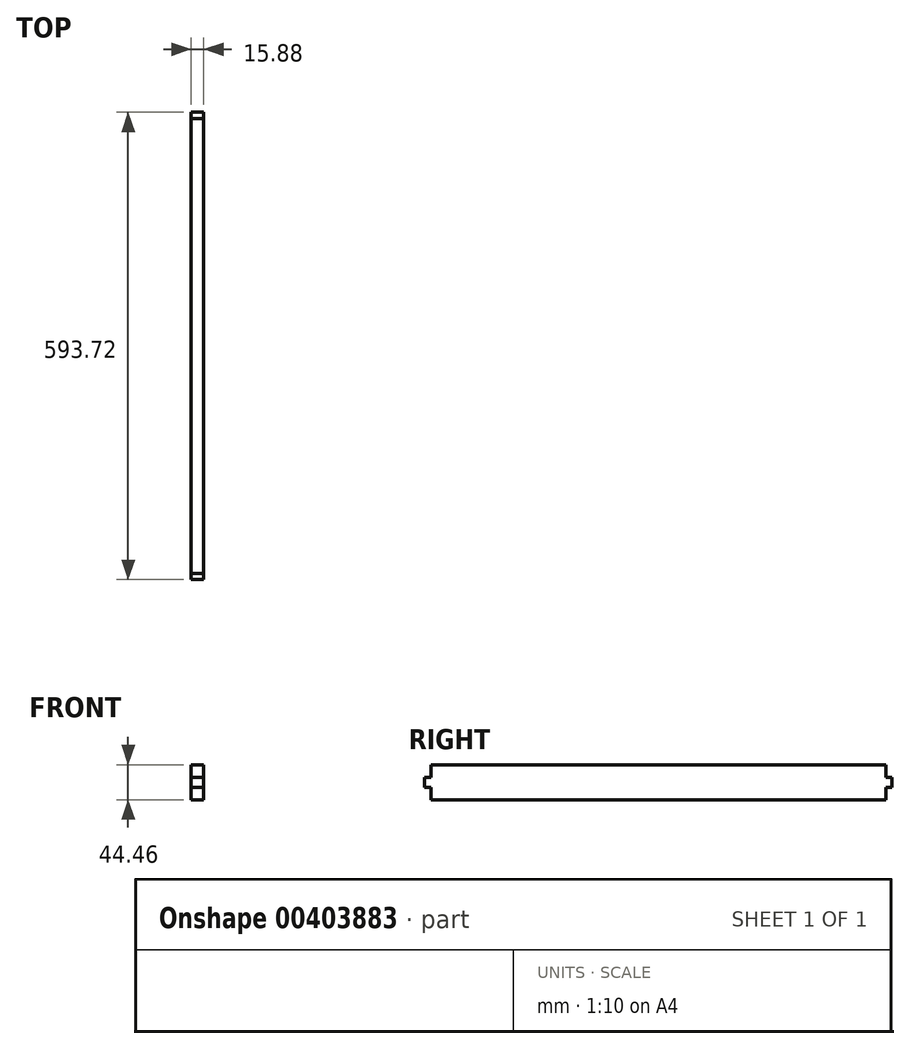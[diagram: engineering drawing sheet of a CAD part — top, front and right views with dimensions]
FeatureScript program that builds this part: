
annotation { "Feature Type Name" : "Feature", "Feature Type Description" : "" }
export const myFeature = defineFeature(function(context is Context, id is Id, definition is map)
    precondition{}
    {
        {
            var Q0;
            Q0=qCreatedBy(makeId("Right.planeOp"),FACE);
            var sketch = newSketch(context, id + "F0", { "sketchPlane" : qUnion([Q0])});
            skLineSegment(sketch, "E0.bottom", {"start": v(296.86, -22.23) * mm, "end": v(-296.86, -22.23) * mm});
            skLineSegment(sketch, "E0.top", {"start": v(296.86, 22.23) * mm, "end": v(-296.86, 22.22) * mm});
            skLineSegment(sketch, "E0.left", {"start": v(296.86, -22.23) * mm, "end": v(296.86, 22.22) * mm});
            skLineSegment(sketch, "E0.right", {"start": v(-296.86, -22.23) * mm, "end": v(-296.86, 22.22) * mm});
            skPoint(sketch, "E0.middle", {"position": v(0, 0) * mm});
            skSolve(sketch);
        }
        {
            var Q0;
            Q0 = qSketchRegion(id + "F0", true);
            extrude(context, id + "F1", {"entities" : qUnion([Q0]), "depth" : 15.88 * mm});
        }
        {
            var Q0;
            Q0=makeQuery(id+"F1.opExtrude","CAP_FACE",FACE,{"disambiguationData":[OSD([sQuery(id+"F0.wireOp",EDGE,"E0.bottom"),sQuery(id+"F0.wireOp",EDGE,"E0.top"),sQuery(id+"F0.wireOp",EDGE,"E0.left"),sQuery(id+"F0.wireOp",EDGE,"E0.right")])],"isStart":false});
            var sketch = newSketch(context, id + "F2", { "sketchPlane" : qUnion([Q0])});
            skLineSegment(sketch, "E1.bottom", {"start": v(-296.86, 22.22) * mm, "end": v(-288.93, 22.22) * mm});
            skLineSegment(sketch, "E1.top", {"start": v(-296.86, 6.35) * mm, "end": v(-288.93, 6.35) * mm});
            skLineSegment(sketch, "E1.left", {"start": v(-296.86, 22.22) * mm, "end": v(-296.86, 6.35) * mm});
            skLineSegment(sketch, "E1.right", {"start": v(-288.93, 22.22) * mm, "end": v(-288.93, 6.35) * mm});
            skLineSegment(sketch, "E2.bottom", {"start": v(-296.86, -22.23) * mm, "end": v(-288.93, -22.23) * mm});
            skLineSegment(sketch, "E2.top", {"start": v(-296.86, -6.35) * mm, "end": v(-288.93, -6.35) * mm});
            skLineSegment(sketch, "E2.left", {"start": v(-296.86, -22.23) * mm, "end": v(-296.86, -6.35) * mm});
            skLineSegment(sketch, "E2.right", {"start": v(-288.93, -22.23) * mm, "end": v(-288.93, -6.35) * mm});
            skLineSegment(sketch, "E3.MirrorCS", {"start": v(296.86, 22.22) * mm, "end": v(288.93, 22.22) * mm});
            skLineSegment(sketch, "E4.MirrorCS", {"start": v(296.86, 6.35) * mm, "end": v(288.93, 6.35) * mm});
            skLineSegment(sketch, "E5.MirrorCS", {"start": v(288.93, -22.23) * mm, "end": v(288.93, -6.35) * mm});
            skLineSegment(sketch, "E6.MirrorCS", {"start": v(296.86, 22.22) * mm, "end": v(296.86, 6.35) * mm});
            skLineSegment(sketch, "E7.MirrorCS", {"start": v(288.93, 22.22) * mm, "end": v(288.93, 6.35) * mm});
            skLineSegment(sketch, "E8.MirrorCS", {"start": v(296.86, -22.23) * mm, "end": v(288.93, -22.23) * mm});
            skLineSegment(sketch, "E9.MirrorCS", {"start": v(296.86, -22.23) * mm, "end": v(296.86, -6.35) * mm});
            skLineSegment(sketch, "E10.MirrorCS", {"start": v(296.86, -6.35) * mm, "end": v(288.93, -6.35) * mm});
            skSolve(sketch);
        }
        {
            var Q0;
            Q0 = qSketchRegion(id + "F2", true);
            extrude(context, id + "F3", {"entities" : qUnion([Q0]), "operationType" : NewBodyOperationType.REMOVE, "oppositeDirection" : true, "depth" : 25.4 * mm});
        }
    });
